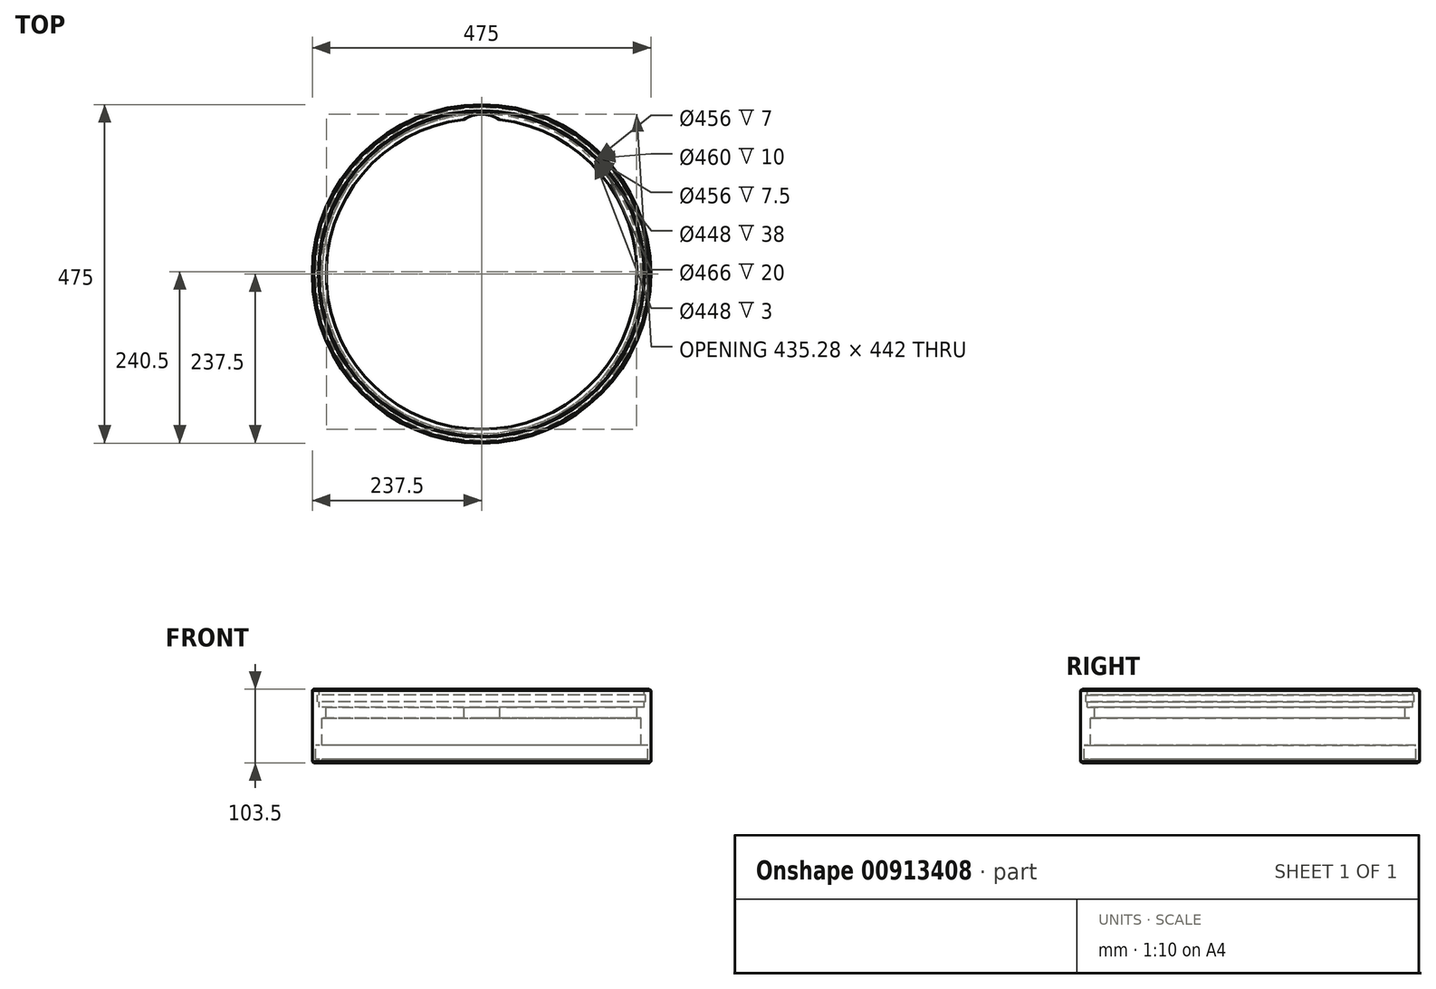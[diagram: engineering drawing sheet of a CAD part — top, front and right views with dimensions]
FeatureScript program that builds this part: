
annotation { "Feature Type Name" : "Feature", "Feature Type Description" : "" }
export const myFeature = defineFeature(function(context is Context, id is Id, definition is map)
    precondition{}
    {
        {
            var Q0;
            Q0=qCreatedBy(makeId("Front.planeOp"),FACE);
            var sketch = newSketch(context, id + "F0", { "sketchPlane" : qUnion([Q0])});
            skLineSegment(sketch, "E0", {"start": v(-24.7, 0) * mm, "end": v(241.44, 0) * mm, "construction": true});
            skLineSegment(sketch, "E1", {"start": v(0, 33.53) * mm, "end": v(0, -114.19) * mm, "construction": true});
            skLineSegment(sketch, "E2.0", {"start": v(237.5, 33.53) * mm, "end": v(237.5, -103.5) * mm});
            skLineSegment(sketch, "E3.0", {"start": v(-24.7, -103.5) * mm, "end": v(241.44, -103.5) * mm});
            skLineSegment(sketch, "E4", {"start": v(237.5, 0) * mm, "end": v(114.18, 0) * mm});
            skLineSegment(sketch, "E5", {"start": v(228, 0) * mm, "end": v(228, -8) * mm});
            skLineSegment(sketch, "E6", {"start": v(228, -8) * mm, "end": v(230, -8) * mm});
            skLineSegment(sketch, "E7", {"start": v(230, -8) * mm, "end": v(230, -18) * mm});
            skLineSegment(sketch, "E8", {"start": v(230, -18) * mm, "end": v(228, -18) * mm});
            skLineSegment(sketch, "E9", {"start": v(228, -18) * mm, "end": v(228, -25.5) * mm});
            skLineSegment(sketch, "E10", {"start": v(228, -25.5) * mm, "end": v(218, -25.5) * mm});
            skLineSegment(sketch, "E11", {"start": v(218, -25.5) * mm, "end": v(218, -40.5) * mm});
            skLineSegment(sketch, "E12", {"start": v(218, -40.5) * mm, "end": v(224, -40.5) * mm});
            skLineSegment(sketch, "E13", {"start": v(224, -78.5) * mm, "end": v(233, -78.5) * mm});
            skLineSegment(sketch, "E14", {"start": v(233, -78.5) * mm, "end": v(233, -98.5) * mm});
            skLineSegment(sketch, "E15", {"start": v(233, -98.5) * mm, "end": v(224, -98.5) * mm});
            skLineSegment(sketch, "E16", {"start": v(224, -98.5) * mm, "end": v(224, -103.5) * mm});
            skLineSegment(sketch, "E17", {"start": v(224, -40.5) * mm, "end": v(224, -78.5) * mm});
            skSolve(sketch);
        }
        {
            var Q0;
            {var subQ6=sQuery(id+"F0.wireOp",EDGE,"E5");Q0=makeQuery(id+"F0.imprint","IMPRINT",FACE,{"disambiguationData":[TD([[makeQuery(id+"F0.imprint","IMPRINT",EDGE,{"derivedFrom":subQ6}),1.0]])]});}
            var Q1;
            Q1=sQuery(id+"F0.wireOp",EDGE,"E1");
            revolve(context, id + "F1", {"surfaceOperationType" : NewSurfaceOperationType.NEW, "entities" : qUnion([Q0]), "axis" : qUnion([Q1]), "revolveType" : RevolveType.FULL});
        }
        {
            var Q0;
            Q0=makeQuery(id+"F1.opRevolve","SWEPT_EDGE",EDGE,{"disambiguationData":[OSD([sQuery(id+"F0.wireOp",EDGE,"E4"),sQuery(id+"F0.wireOp",EDGE,"E5")])]});
            chamfer(context, id + "F2", {"entities" : qUnion([Q0]), "width" : 1 * mm, "tangentPropagation" : true});
        }
        {
            var Q0;
            Q0=makeQuery(id+"F1.opRevolve","SWEPT_EDGE",EDGE,{"disambiguationData":[OSD([sQuery(id+"F0.wireOp",EDGE,"E2.0"),sQuery(id+"F0.wireOp",EDGE,"E4")])]});
            var Q1;
            Q1=makeQuery(id+"F1.opRevolve","SWEPT_EDGE",EDGE,{"disambiguationData":[OSD([sQuery(id+"F0.wireOp",EDGE,"E3.0"),sQuery(id+"F0.wireOp",EDGE,"E16")])]});
            var Q2;
            Q2=makeQuery(id+"F1.opRevolve","SWEPT_EDGE",EDGE,{"disambiguationData":[OSD([sQuery(id+"F0.wireOp",EDGE,"E2.0"),sQuery(id+"F0.wireOp",EDGE,"E3.0")])]});
            chamfer(context, id + "F3", {"entities" : qUnion([Q0, Q1, Q2]), "width" : 2 * mm, "tangentPropagation" : true});
        }
        {
            var Q0;
            Q0=qCreatedBy(makeId("Top.planeOp"),FACE);
            var sketch = newSketch(context, id + "F4", { "sketchPlane" : qUnion([Q0])});
            skLineSegment(sketch, "E18", {"start": v(0, 240.4) * mm, "end": v(0, -53.58) * mm, "construction": true});
            skArc(sketch, "E19", {"start": v(25, 216.56) * mm, "mid": v(0, 218) * mm, "end": v(-25, 216.56) * mm});
            skArc(sketch, "E20", {"start": v(25, 216.56) * mm, "mid": v(0, 224) * mm, "end": v(-25, 216.56) * mm});
            skLineSegment(sketch, "E21", {"start": v(136.56, 0) * mm, "end": v(-107.42, 0) * mm, "construction": true});
            skArc(sketch, "E22.MirrorCS", {"start": v(25, -216.56) * mm, "mid": v(0, -224) * mm, "end": v(-25, -216.56) * mm});
            skArc(sketch, "E23.MirrorCS", {"start": v(25, -216.56) * mm, "mid": v(0, -218) * mm, "end": v(-25, -216.56) * mm});
            skSolve(sketch);
        }
        {
            var Q0;
            Q0=makeQuery(id+"F4.imprint","IMPRINT",FACE,{"disambiguationData":[TD([[makeQuery(id+"F4.imprint","IMPRINT",EDGE,{"derivedFrom":sQuery(id+"F4.wireOp",EDGE,"E19")}),-1.0]])]});
            var Q1;
            Q1=makeQuery(id+"F4.imprint","IMPRINT",FACE,{"disambiguationData":[TD([[makeQuery(id+"F4.imprint","IMPRINT",EDGE,{"derivedFrom":sQuery(id+"F4.wireOp",EDGE,"E22.MirrorCS")}),-1.0]])]});
            extrude(context, id + "F5", {"entities" : qUnion([Q0, Q1]), "operationType" : NewBodyOperationType.REMOVE, "endBound" : BoundingType.SYMMETRIC, "depth" : 200 * mm, "offsetDistance" : 25 * mm});
        }
    });
